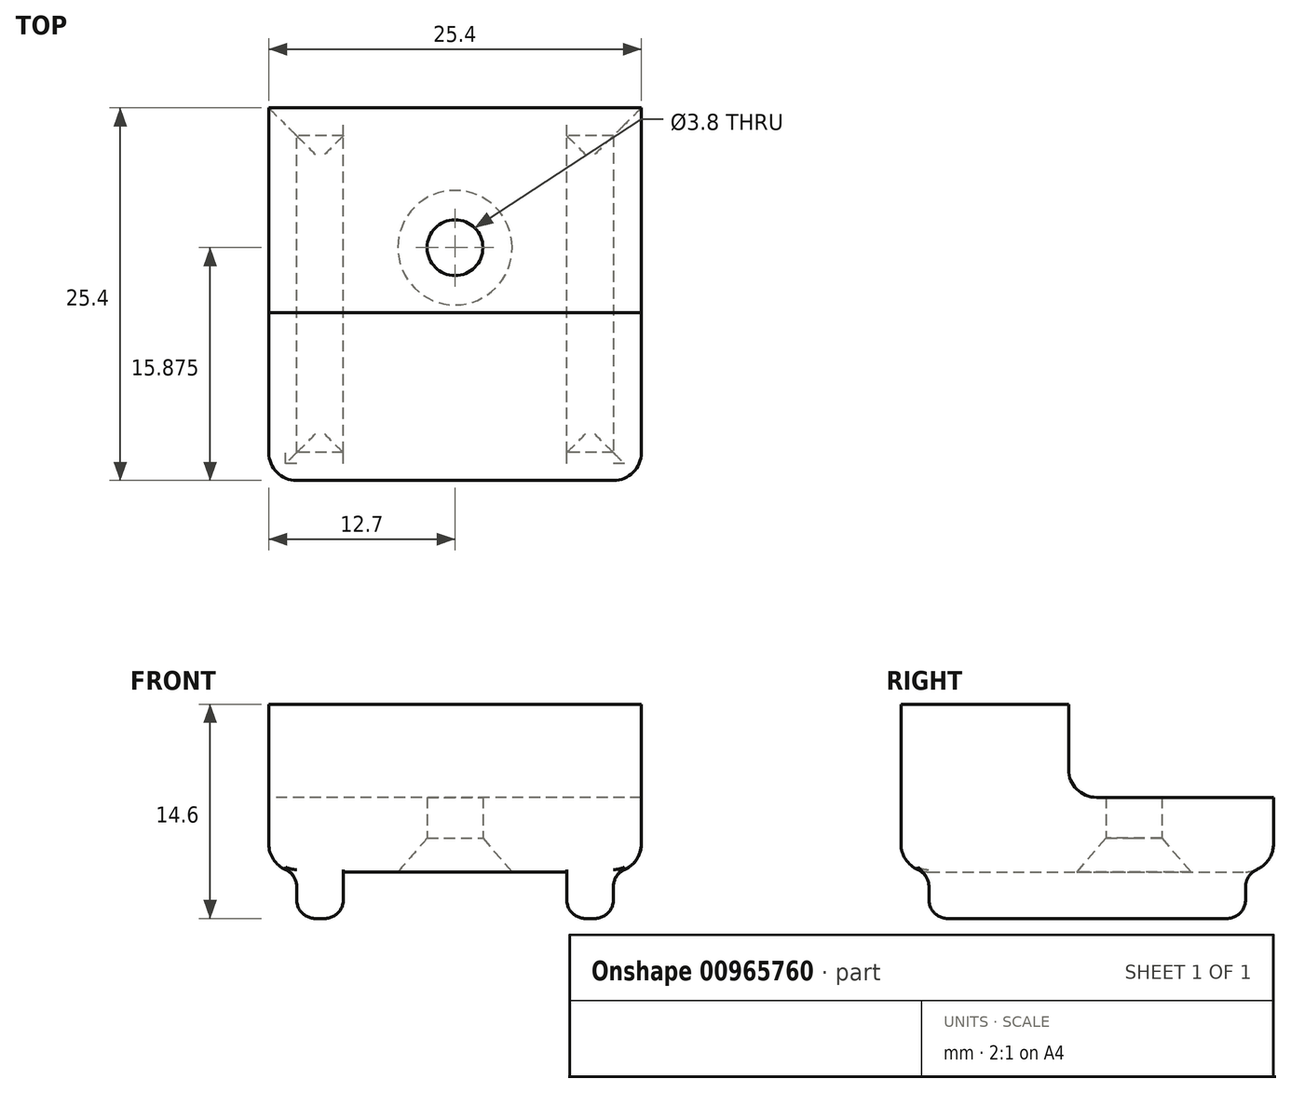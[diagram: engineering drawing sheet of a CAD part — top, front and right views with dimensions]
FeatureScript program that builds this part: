
annotation { "Feature Type Name" : "Feature", "Feature Type Description" : "" }
export const myFeature = defineFeature(function(context is Context, id is Id, definition is map)
    precondition{}
    {
        {
            var Q0;
            Q0=qCreatedBy(makeId("Right.planeOp"),FACE);
            var sketch = newSketch(context, id + "F0", { "sketchPlane" : qUnion([Q0])});
            skLineSegment(sketch, "E0", {"start": v(0, 11.43) * mm, "end": v(0, 0) * mm});
            skLineSegment(sketch, "E1", {"start": v(0, 0) * mm, "end": v(25.4, 0) * mm});
            skLineSegment(sketch, "E2", {"start": v(25.4, 0) * mm, "end": v(25.4, 5.08) * mm});
            skLineSegment(sketch, "E3", {"start": v(25.4, 5.08) * mm, "end": v(11.43, 5.08) * mm});
            skLineSegment(sketch, "E4", {"start": v(11.43, 5.08) * mm, "end": v(11.43, 11.43) * mm});
            skLineSegment(sketch, "E5", {"start": v(11.43, 11.43) * mm, "end": v(0, 11.43) * mm});
            skSolve(sketch);
        }
        {
            var Q0;
            Q0=makeQuery(id+"F0.imprint","IMPRINT",FACE,{"disambiguationData":[TD([[makeQuery(id+"F0.imprint","IMPRINT",EDGE,{"derivedFrom":sQuery(id+"F0.wireOp",EDGE,"E0")}),1.0]])]});
            extrude(context, id + "F1", {"entities" : qUnion([Q0]), "depth" : 25.4 * mm, "offsetDistance" : 25.4 * mm});
        }
        {
            var Q0;
            Q0=makeQuery(id+"F1.opExtrude","SWEPT_FACE",FACE,{"disambiguationData":[OSD([sQuery(id+"F0.wireOp",EDGE,"E1")])]});
            var sketch = newSketch(context, id + "F2", { "sketchPlane" : qUnion([Q0])});
            skPoint(sketch, "E6", {"position": v(12.7, -15.88) * mm});
            skPoint(sketch, "E6.positionSnap0", {"position": v(12.7, -25.4) * mm});
            skSolve(sketch);
        }
        {
            var Q0;
            Q0=sQuery(id+"F2.wireOp",VERTEX,"E6");
            var Q1;
            Q1=makeQuery(id+"F1.opExtrude","SWEPT_BODY",BODY,{"disambiguationData":[OSD([sQuery(id+"F0.wireOp",EDGE,"E0"),sQuery(id+"F0.wireOp",EDGE,"E1"),sQuery(id+"F0.wireOp",EDGE,"E2"),sQuery(id+"F0.wireOp",EDGE,"E3"),sQuery(id+"F0.wireOp",EDGE,"E4"),sQuery(id+"F0.wireOp",EDGE,"E5")])]});
            hole(context, id + "F3", {"style" : HoleStyle.C_SINK, "endStyle" : HoleEndStyle.THROUGH, "standardTappedOrClearance" : lookupTablePath({ "fit" : "Free", "standard" : "ANSI", "size" : "#6", "type" : "Clearance" }), "standardBlindInLast" : lookupTablePath({ "fit" : "Free", "standard" : "ANSI", "size" : "#6", "type" : "Clearance" }), "holeDiameter" : 3.8 * mm, "cSinkDiameter" : 7.8 * mm, "cSinkAngle" : 82 * degree, "majorDiameter" : 6.35 * mm, "isTappedThrough" : true, "tappedDepth" : 19.05 * mm, "tapClearance" : 3, "locations" : qUnion([Q0]), "scope" : qUnion([Q1])});
        }
        {
            var Q0;
            Q0=makeQuery(id+"F1.opExtrude","SWEPT_EDGE",EDGE,{"disambiguationData":[OSD([sQuery(id+"F0.wireOp",EDGE,"E3"),sQuery(id+"F0.wireOp",EDGE,"E4")])]});
            var Q1;
            Q1=makeQuery(id+"F1.opExtrude","SWEPT_EDGE",EDGE,{"disambiguationData":[OSD([sQuery(id+"F0.wireOp",EDGE,"E0"),sQuery(id+"F0.wireOp",EDGE,"E1")])]});
            var Q2;
            Q2=makeQuery(id+"F1.opExtrude","SWEPT_EDGE",EDGE,{"disambiguationData":[OSD([sQuery(id+"F0.wireOp",EDGE,"E1"),sQuery(id+"F0.wireOp",EDGE,"E2")])]});
            var Q3;
            Q3=makeQuery(id+"F1.opExtrude","CAP_EDGE",EDGE,{"disambiguationData":[OSD([sQuery(id+"F0.wireOp",EDGE,"E1")])],"isStart":false});
            var Q4;
            Q4=makeQuery(id+"F1.opExtrude","CAP_EDGE",EDGE,{"disambiguationData":[OSD([sQuery(id+"F0.wireOp",EDGE,"E1")])],"isStart":true});
            var Q5;
            Q5=makeQuery(id+"F1.opExtrude","CAP_EDGE",EDGE,{"disambiguationData":[OSD([sQuery(id+"F0.wireOp",EDGE,"E0")])],"isStart":false});
            var Q6;
            Q6=makeQuery(id+"F1.opExtrude","CAP_EDGE",EDGE,{"disambiguationData":[OSD([sQuery(id+"F0.wireOp",EDGE,"E0")])],"isStart":true});
            fillet(context, id + "F4", {"entities" : qUnion([Q0, Q1, Q2, Q3, Q4, Q5, Q6]), "radius" : 1.9 * mm, "tangentPropagation" : true, "allowEdgeOverflow" : false});
        }
        {
            var Q0;
            Q0=makeQuery(id+"F1.opExtrude","SWEPT_FACE",FACE,{"disambiguationData":[OSD([sQuery(id+"F0.wireOp",EDGE,"E1")])]});
            var sketch = newSketch(context, id + "F5", { "sketchPlane" : qUnion([Q0])});
            skLineSegment(sketch, "E7.bottom", {"start": v(23.5, -1.9) * mm, "end": v(20.32, -1.9) * mm});
            skLineSegment(sketch, "E7.top", {"start": v(23.5, -23.5) * mm, "end": v(20.32, -23.5) * mm});
            skLineSegment(sketch, "E7.left", {"start": v(23.5, -1.9) * mm, "end": v(23.5, -23.5) * mm});
            skLineSegment(sketch, "E7.right", {"start": v(20.32, -1.9) * mm, "end": v(20.32, -23.5) * mm});
            skLineSegment(sketch, "E8.bottom", {"start": v(1.9, -1.9) * mm, "end": v(5.08, -1.9) * mm});
            skLineSegment(sketch, "E8.top", {"start": v(1.9, -23.5) * mm, "end": v(5.08, -23.5) * mm});
            skLineSegment(sketch, "E8.left", {"start": v(1.9, -1.9) * mm, "end": v(1.9, -23.5) * mm});
            skLineSegment(sketch, "E8.right", {"start": v(5.08, -1.9) * mm, "end": v(5.08, -23.5) * mm});
            skSolve(sketch);
        }
        {
            var Q0;
            Q0 = qSketchRegion(id + "F5", true);
            extrude(context, id + "F6", {"entities" : qUnion([Q0]), "operationType" : NewBodyOperationType.ADD, "depth" : 3.17 * mm, "offsetDistance" : 25.4 * mm});
        }
        {
            var Q0;
            Q0=makeQuery(id+"F6.opExtrude","CAP_FACE",FACE,{"disambiguationData":[OSD([sQuery(id+"F5.wireOp",EDGE,"E7.bottom"),sQuery(id+"F5.wireOp",EDGE,"E7.top"),sQuery(id+"F5.wireOp",EDGE,"E7.left"),sQuery(id+"F5.wireOp",EDGE,"E7.right")])],"isStart":false});
            var Q1;
            Q1=makeQuery(id+"F6.opExtrude","CAP_FACE",FACE,{"disambiguationData":[OSD([sQuery(id+"F5.wireOp",EDGE,"E8.bottom"),sQuery(id+"F5.wireOp",EDGE,"E8.top"),sQuery(id+"F5.wireOp",EDGE,"E8.left"),sQuery(id+"F5.wireOp",EDGE,"E8.right")])],"isStart":false});
            var Q2;
            {var subQ0=sQuery(id+"F0.wireOp",EDGE,"E1");Q2=makeQuery(id+"F6.boolean.opBoolean","MERGE",EDGE,{"derivedFrom":[makeQuery(id+"F4.opFillet","BLEND_EDGE",EDGE,{"blendedFrom":[makeQuery(id+"F1.opExtrude","CAP_EDGE",EDGE,{"disambiguationData":[OSD([subQ0])],"isStart":false}),makeQuery(id+"F1.opExtrude","SWEPT_FACE",FACE,{"disambiguationData":[OSD([subQ0])]})],"blendedInto":[makeQuery(id+"F1.opExtrude","SWEPT_FACE",FACE,{"disambiguationData":[OSD([subQ0])]})]}),makeQuery(id+"F6.opExtrude","CAP_EDGE",EDGE,{"disambiguationData":[OSD([sQuery(id+"F5.wireOp",EDGE,"E7.left")])],"isStart":true})]});}
            var Q3;
            {var subQ0=sQuery(id+"F0.wireOp",EDGE,"E1");Q3=makeQuery(id+"F6.boolean.opBoolean","MERGE",EDGE,{"derivedFrom":[makeQuery(id+"F4.opFillet","BLEND_EDGE",EDGE,{"blendedFrom":[makeQuery(id+"F1.opExtrude","SWEPT_EDGE",EDGE,{"disambiguationData":[OSD([sQuery(id+"F0.wireOp",EDGE,"E0"),subQ0])]}),makeQuery(id+"F1.opExtrude","SWEPT_FACE",FACE,{"disambiguationData":[OSD([subQ0])]})],"blendedInto":[makeQuery(id+"F1.opExtrude","SWEPT_FACE",FACE,{"disambiguationData":[OSD([subQ0])]})]}),makeQuery(id+"F6.opExtrude","CAP_EDGE",EDGE,{"disambiguationData":[OSD([sQuery(id+"F5.wireOp",EDGE,"E7.bottom")])],"isStart":true})]});}
            var Q4;
            {var subQ0=sQuery(id+"F0.wireOp",EDGE,"E1");Q4=makeQuery(id+"F6.boolean.opBoolean","MERGE",EDGE,{"derivedFrom":[makeQuery(id+"F4.opFillet","BLEND_EDGE",EDGE,{"blendedFrom":[makeQuery(id+"F1.opExtrude","SWEPT_EDGE",EDGE,{"disambiguationData":[OSD([sQuery(id+"F0.wireOp",EDGE,"E0"),subQ0])]}),makeQuery(id+"F1.opExtrude","SWEPT_FACE",FACE,{"disambiguationData":[OSD([subQ0])]})],"blendedInto":[makeQuery(id+"F1.opExtrude","SWEPT_FACE",FACE,{"disambiguationData":[OSD([subQ0])]})]}),makeQuery(id+"F6.opExtrude","CAP_EDGE",EDGE,{"disambiguationData":[OSD([sQuery(id+"F5.wireOp",EDGE,"E8.bottom")])],"isStart":true})]});}
            var Q5;
            Q5=makeQuery(id+"F6.opExtrude","CAP_EDGE",EDGE,{"disambiguationData":[OSD([sQuery(id+"F5.wireOp",EDGE,"E8.right")])],"isStart":true});
            var Q6;
            Q6=makeQuery(id+"F6.opExtrude","CAP_EDGE",EDGE,{"disambiguationData":[OSD([sQuery(id+"F5.wireOp",EDGE,"E7.right")])],"isStart":true});
            var Q7;
            {var subQ0=sQuery(id+"F0.wireOp",EDGE,"E1");Q7=makeQuery(id+"F6.boolean.opBoolean","MERGE",EDGE,{"derivedFrom":[makeQuery(id+"F4.opFillet","BLEND_EDGE",EDGE,{"blendedFrom":[makeQuery(id+"F1.opExtrude","SWEPT_EDGE",EDGE,{"disambiguationData":[OSD([subQ0,sQuery(id+"F0.wireOp",EDGE,"E2")])]}),makeQuery(id+"F1.opExtrude","SWEPT_FACE",FACE,{"disambiguationData":[OSD([subQ0])]})],"blendedInto":[makeQuery(id+"F1.opExtrude","SWEPT_FACE",FACE,{"disambiguationData":[OSD([subQ0])]})]}),makeQuery(id+"F6.opExtrude","CAP_EDGE",EDGE,{"disambiguationData":[OSD([sQuery(id+"F5.wireOp",EDGE,"E7.top")])],"isStart":true})]});}
            var Q8;
            {var subQ0=sQuery(id+"F0.wireOp",EDGE,"E1");Q8=makeQuery(id+"F6.boolean.opBoolean","MERGE",EDGE,{"derivedFrom":[makeQuery(id+"F4.opFillet","BLEND_EDGE",EDGE,{"blendedFrom":[makeQuery(id+"F1.opExtrude","SWEPT_EDGE",EDGE,{"disambiguationData":[OSD([subQ0,sQuery(id+"F0.wireOp",EDGE,"E2")])]}),makeQuery(id+"F1.opExtrude","SWEPT_FACE",FACE,{"disambiguationData":[OSD([subQ0])]})],"blendedInto":[makeQuery(id+"F1.opExtrude","SWEPT_FACE",FACE,{"disambiguationData":[OSD([subQ0])]})]}),makeQuery(id+"F6.opExtrude","CAP_EDGE",EDGE,{"disambiguationData":[OSD([sQuery(id+"F5.wireOp",EDGE,"E8.top")])],"isStart":true})]});}
            var Q9;
            {var subQ0=sQuery(id+"F0.wireOp",EDGE,"E1");Q9=makeQuery(id+"F6.boolean.opBoolean","MERGE",EDGE,{"derivedFrom":[makeQuery(id+"F4.opFillet","BLEND_EDGE",EDGE,{"blendedFrom":[makeQuery(id+"F1.opExtrude","CAP_EDGE",EDGE,{"disambiguationData":[OSD([subQ0])],"isStart":true}),makeQuery(id+"F1.opExtrude","SWEPT_FACE",FACE,{"disambiguationData":[OSD([subQ0])]})],"blendedInto":[makeQuery(id+"F1.opExtrude","SWEPT_FACE",FACE,{"disambiguationData":[OSD([subQ0])]})]}),makeQuery(id+"F6.opExtrude","CAP_EDGE",EDGE,{"disambiguationData":[OSD([sQuery(id+"F5.wireOp",EDGE,"E8.left")])],"isStart":true})]});}
            fillet(context, id + "F7", {"entities" : qUnion([Q0, Q1, Q2, Q3, Q4, Q5, Q6, Q7, Q8, Q9]), "radius" : 1.27 * mm, "tangentPropagation" : true, "allowEdgeOverflow" : false});
        }
    });
